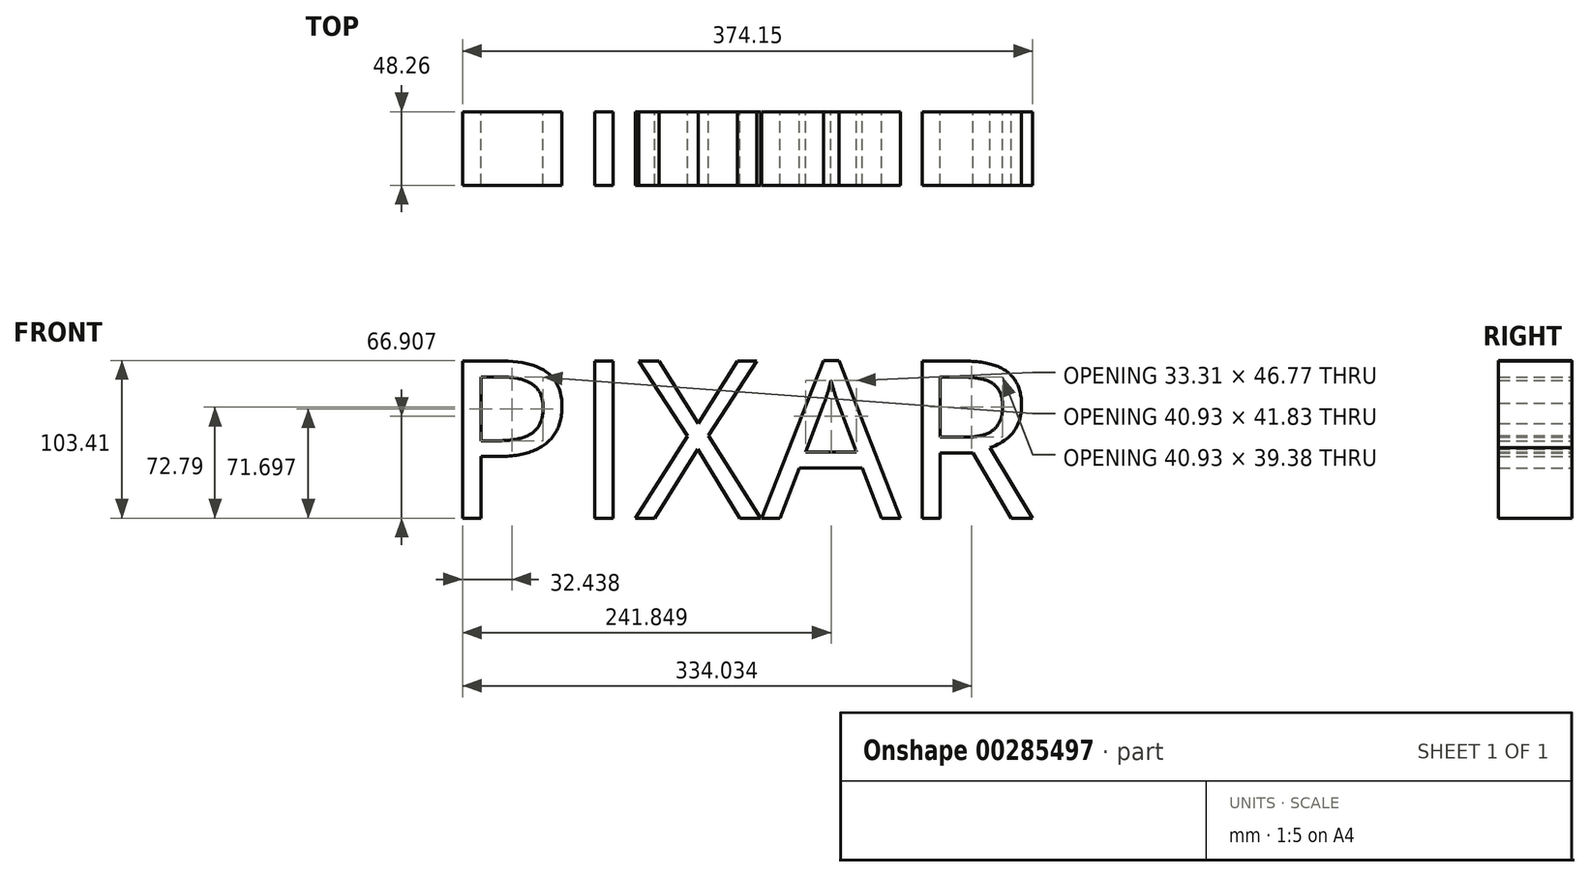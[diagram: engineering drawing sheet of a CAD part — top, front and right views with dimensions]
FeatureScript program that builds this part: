
annotation { "Feature Type Name" : "Feature", "Feature Type Description" : "" }
export const myFeature = defineFeature(function(context is Context, id is Id, definition is map)
    precondition{}
    {
        {
            var Q0;
            Q0=qCreatedBy(makeId("Front.planeOp"),FACE);
            var sketch = newSketch(context, id + "F0", { "sketchPlane" : qUnion([Q0])});
            skText(sketch, "E0", { "text": "PIXAR\n", "fontName": "OpenSans-Regular.ttf"});
            const initialGuessF0  = {"E0": [-0.06651, -0.03627, 1, 0, 0.10386]};
            skSetInitialGuess(sketch, initialGuessF0);
            skSolve(sketch);
        }
        {
            var Q0;
            Q0 = qSketchRegion(id + "F0", true);
            extrude(context, id + "F1", {"entities" : qUnion([Q0]), "depth" : 48.26 * mm});
        }
    });
